# Revit family: Solo tukikahva
name_source: partatom
category: Casework
revit_build: Autodesk Revit 2015 (Build: 20140606_1530(x64)
units: mm (PartAtom-declared; Revit-internal decimal feet)

## types (6) — shared parameters
Manufacturer = Korpinen
Model = Solo tukikahva
URL = http://www.korpinen.com
zero-valued in all types: NominalDepth, NominalHeight, NominalLength

## per-type parameters (varying)
| type | Depth | Height | Keynote | Solo tuikkahva | Width |
| Solo tukikahva 16802 W | 98 mm  [stored 0.321522 ft] | 74 mm  [stored 0.242782 ft] | 16802 | 01 Solo tuikkahva 16802 : Solo tuikkahva 16802 W | 800 mm  [stored 2.62467 ft] |
| Solo tukikahva 16802 R | 98 mm  [stored 0.321522 ft] | 74 mm  [stored 0.242782 ft] | 16802 | 01 Solo tuikkahva 16802 : Solo tuikkahva 16802 R | 800 mm  [stored 2.62467 ft] |
| Solo tukikahva 16802 G | 98 mm  [stored 0.321522 ft] | 74 mm  [stored 0.242782 ft] | 16802 | 01 Solo tuikkahva 16802 : Solo tuikkahva 16802 G | 800 mm  [stored 2.62467 ft] |
| Solo tukikahva 16804 W | 94 mm  [stored 0.308399 ft] | 1200 mm | 16804 | 01 Solo tuikkahva 16804 : Solo tuikkahva 16804 W | 74 mm  [stored 0.242782 ft] |
| Solo tukikahva 16804 R | 94 mm  [stored 0.308399 ft] | 1200 mm | 16804 | 01 Solo tuikkahva 16804 : Solo tuikkahva 16804 R | 74 mm  [stored 0.242782 ft] |
| Solo tukikahva 16804 G | 94 mm  [stored 0.308399 ft] | 1200 mm | 16804 | 01 Solo tuikkahva 16804 : Solo tuikkahva 16804 G | 74 mm  [stored 0.242782 ft] |

note: [stored X ft] marks values corroborated as IEEE doubles in the binary element streams (Revit-internal decimal feet)

## geometry (parser evidence)
native form markers: Blend x4, Sweep x12
no freeform markers — native parametric forms only
